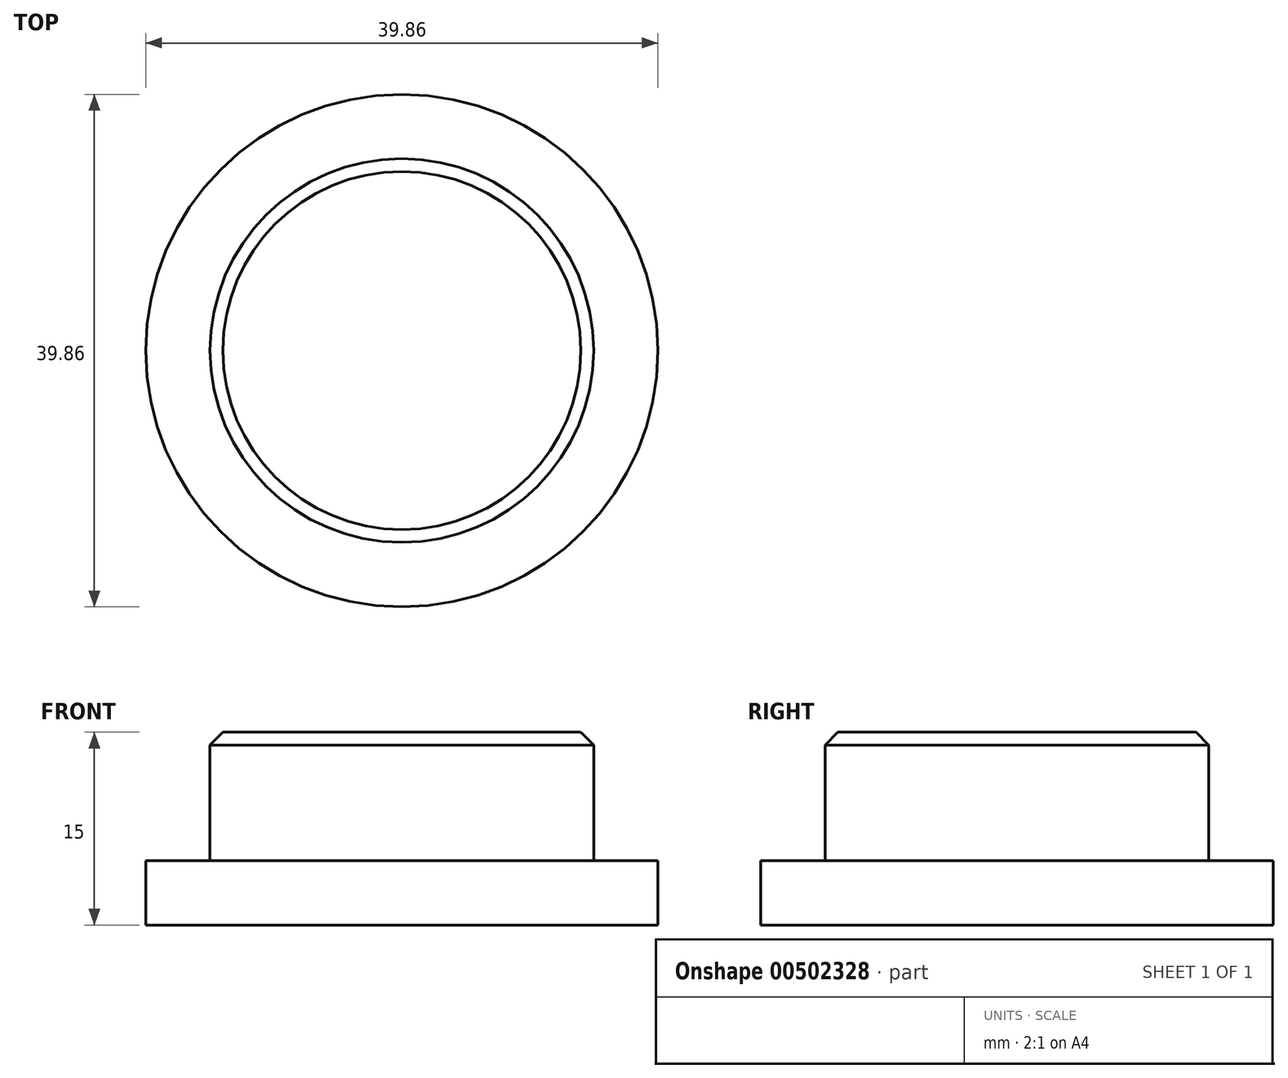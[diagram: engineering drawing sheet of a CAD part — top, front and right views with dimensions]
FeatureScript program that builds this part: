
annotation { "Feature Type Name" : "Feature", "Feature Type Description" : "" }
export const myFeature = defineFeature(function(context is Context, id is Id, definition is map)
    precondition{}
    {
        {
            var Q0;
            Q0=qCreatedBy(makeId("Top.planeOp"),FACE);
            var sketch = newSketch(context, id + "F0", { "sketchPlane" : qUnion([Q0])});
            skCircle(sketch, "E0", {"center": v(0, 0) * mm, "radius": 14.93 * mm});
            skCircle(sketch, "E1.0", {"center": v(0, 0) * mm, "radius": 19.93 * mm});
            skSolve(sketch);
        }
        {
            var Q0;
            Q0=qSketchRegion(id+"F0",true);
            var Q1;
            Q1=makeQuery(id+"F0.imprint","IMPRINT",FACE,{"disambiguationData":[TD([[makeQuery(id+"F0.imprint","IMPRINT",EDGE,{"derivedFrom":sQuery(id+"F0.wireOp",EDGE,"E0")}),1.0]])]});
            extrude(context, id + "F1", {"entities" : qUnion([Q0, Q1]), "depth" : 5 * mm});
        }
        {
            var Q0;
            Q0=makeQuery(id+"F0.imprint","IMPRINT",FACE,{"disambiguationData":[TD([[makeQuery(id+"F0.imprint","IMPRINT",EDGE,{"derivedFrom":sQuery(id+"F0.wireOp",EDGE,"E0")}),1.0]])]});
            extrude(context, id + "F2", {"entities" : qUnion([Q0]), "operationType" : NewBodyOperationType.ADD, "depth" : 15 * mm});
        }
        {
            var Q0;
            Q0=makeQuery(id+"F2.opExtrude","CAP_EDGE",EDGE,{"disambiguationData":[OSD([sQuery(id+"F0.wireOp",EDGE,"E0")])],"isStart":false});
            chamfer(context, id + "F3", {"entities" : qUnion([Q0]), "width" : 1 * mm, "tangentPropagation" : true});
        }
    });
